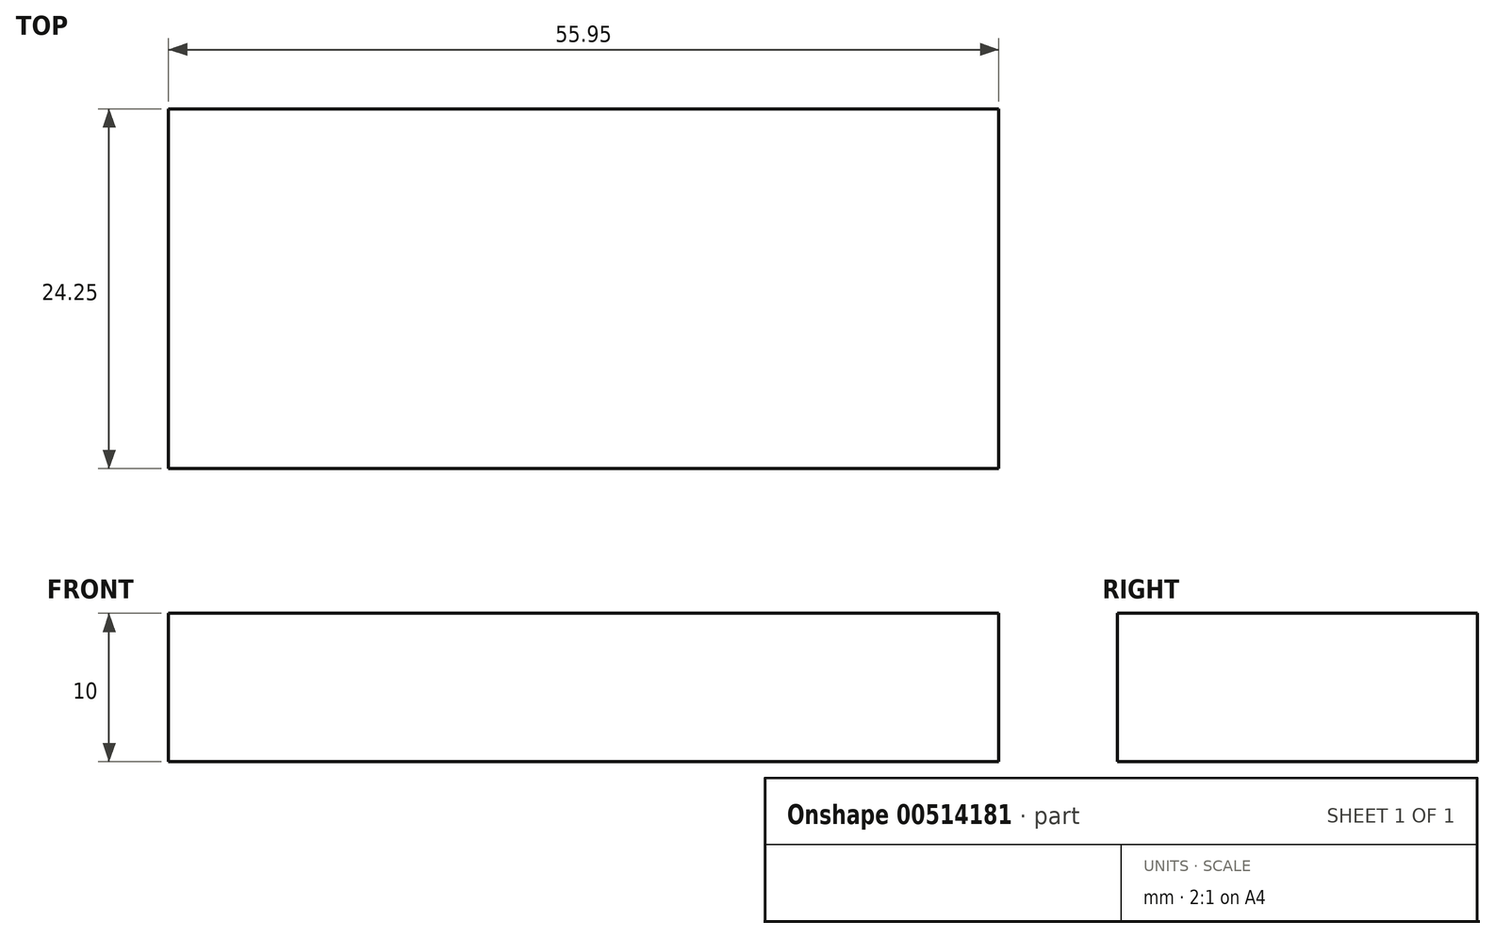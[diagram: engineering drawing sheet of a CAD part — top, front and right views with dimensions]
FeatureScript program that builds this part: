
annotation { "Feature Type Name" : "Feature", "Feature Type Description" : "" }
export const myFeature = defineFeature(function(context is Context, id is Id, definition is map)
    precondition{}
    {
        {
            var Q0;
            Q0=qCreatedBy(makeId("Top.planeOp"),FACE);
            var sketch = newSketch(context, id + "F0", { "sketchPlane" : qUnion([Q0])});
            skLineSegment(sketch, "E0.bottom", {"start": v(0, 0) * mm, "end": v(55.95, 0) * mm});
            skLineSegment(sketch, "E0.top", {"start": v(0, 24.25) * mm, "end": v(55.95, 24.25) * mm});
            skLineSegment(sketch, "E0.left", {"start": v(0, 0) * mm, "end": v(0, 24.25) * mm});
            skLineSegment(sketch, "E0.right", {"start": v(55.95, 0) * mm, "end": v(55.95, 24.25) * mm});
            skSolve(sketch);
        }
        {
            var Q0;
            Q0 = qSketchRegion(id + "F0", true);
            extrude(context, id + "F1", {"entities" : qUnion([Q0]), "depth" : 10 * mm});
        }
    });
